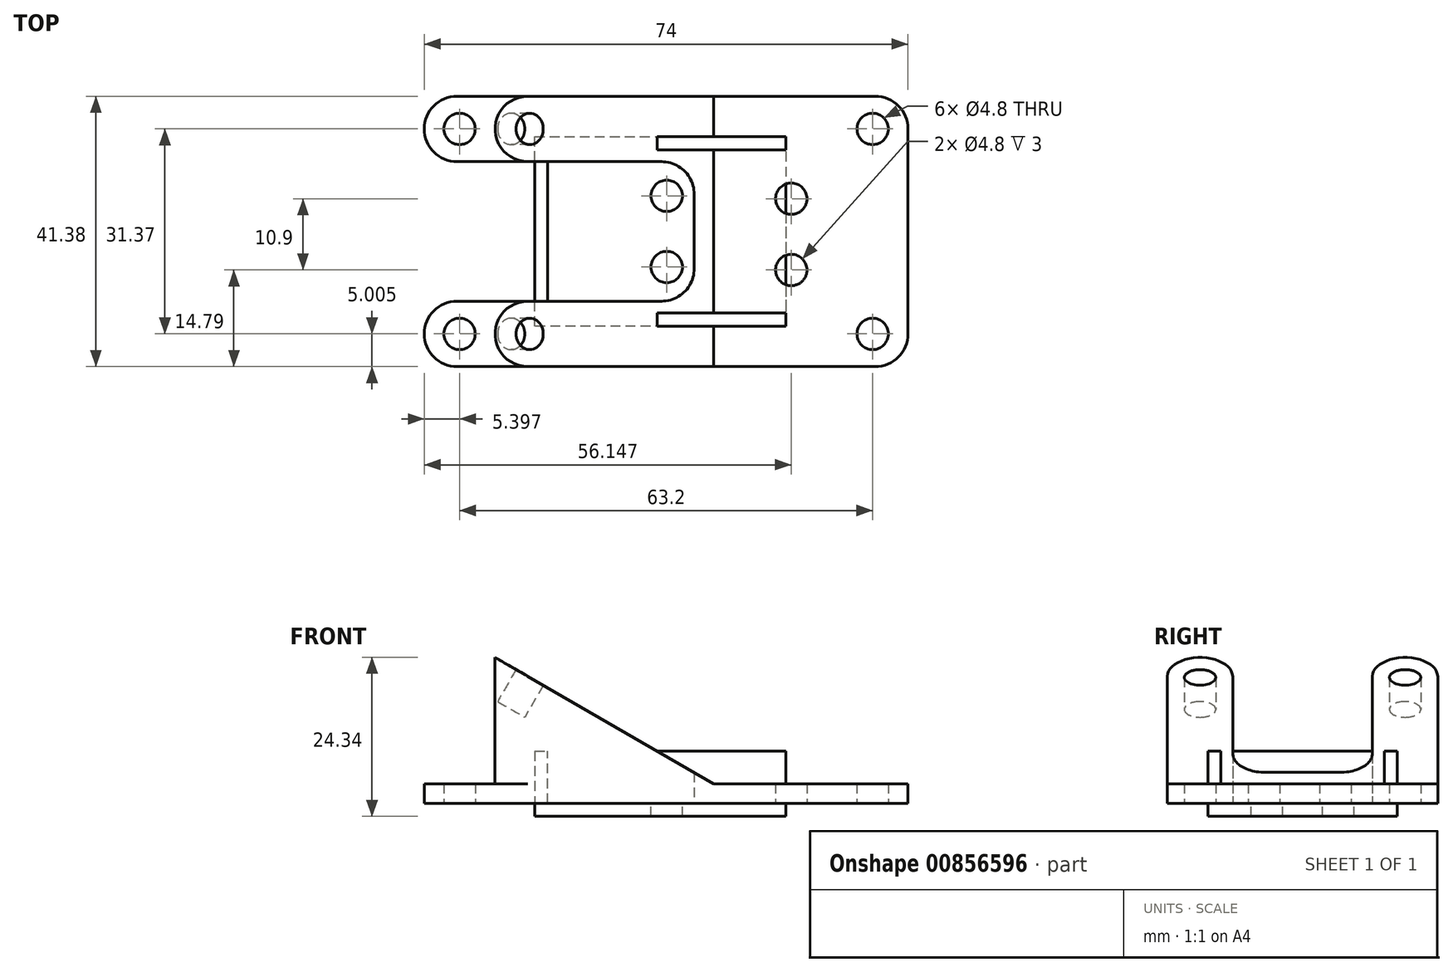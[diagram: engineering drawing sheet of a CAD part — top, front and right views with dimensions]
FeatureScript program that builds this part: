
annotation { "Feature Type Name" : "Feature", "Feature Type Description" : "" }
export const myFeature = defineFeature(function(context is Context, id is Id, definition is map)
    precondition{}
    {
        {
            var Q0;
            Q0=qCreatedBy(makeId("Top.planeOp"),FACE);
            var sketch = newSketch(context, id + "F0", { "sketchPlane" : qUnion([Q0])});
            skPoint(sketch, "E0.middle", {"position": v(0, 0) * mm});
            skCircle(sketch, "E1", {"center": v(-31.7, 15.69) * mm, "radius": 2.4 * mm});
            skLineSegment(sketch, "E2", {"start": v(-29.3, 15.69) * mm, "end": v(30.9, 15.69) * mm, "construction": true});
            skLineSegment(sketch, "E3.right", {"start": v(-37.1, 10.69) * mm, "end": v(-37.1, 20.69) * mm});
            skLineSegment(sketch, "E4", {"start": v(0, 0) * mm, "end": v(-12.47, 0) * mm, "construction": true});
            skLineSegment(sketch, "E5", {"start": v(-30.8, 9.63) * mm, "end": v(4.2, 9.63) * mm, "construction": true});
            skLineSegment(sketch, "E6", {"start": v(-37.1, 10.69) * mm, "end": v(4.2, 10.69) * mm});
            skLineSegment(sketch, "E7", {"start": v(-34.1, 15.69) * mm, "end": v(-37.1, 15.69) * mm, "construction": true});
            skCircle(sketch, "E8", {"center": v(31.5, 15.69) * mm, "radius": 2.4 * mm});
            skLineSegment(sketch, "E9.MirrorCS", {"start": v(-29.3, -15.69) * mm, "end": v(30.9, -15.69) * mm, "construction": true});
            skCircle(sketch, "E10.MirrorC", {"center": v(31.5, -15.69) * mm, "radius": 2.4 * mm});
            skLineSegment(sketch, "E11", {"start": v(33.9, 15.69) * mm, "end": v(36.9, 15.69) * mm, "construction": true});
            skLineSegment(sketch, "E12", {"start": v(-37.1, 20.69) * mm, "end": v(36.9, 20.69) * mm});
            skLineSegment(sketch, "E13.MirrorCS", {"start": v(-37.1, -10.69) * mm, "end": v(-37.1, -20.69) * mm});
            skLineSegment(sketch, "E14.MirrorCS", {"start": v(-37.1, -10.69) * mm, "end": v(4.2, -10.69) * mm});
            skLineSegment(sketch, "E15.MirrorCS", {"start": v(-37.1, -20.69) * mm, "end": v(36.9, -20.69) * mm});
            skLineSegment(sketch, "E16", {"start": v(36.9, 20.69) * mm, "end": v(36.9, -20.69) * mm});
            skLineSegment(sketch, "E17", {"start": v(4.2, 10.69) * mm, "end": v(4.2, -10.69) * mm});
            skLineSegment(sketch, "E18", {"start": v(-31.7, 18.09) * mm, "end": v(-31.7, 20.69) * mm, "construction": true});
            skLineSegment(sketch, "E19", {"start": v(-31.68, 13.29) * mm, "end": v(-31.68, 10.69) * mm, "construction": true});
            skCircle(sketch, "E20.MirrorC", {"center": v(-31.7, -15.69) * mm, "radius": 2.4 * mm});
            skLineSegment(sketch, "E21", {"start": v(4.2, 10.69) * mm, "end": v(4.2, 20.69) * mm});
            skLineSegment(sketch, "E22", {"start": v(4.2, -10.69) * mm, "end": v(4.2, -20.69) * mm});
            skLineSegment(sketch, "E23", {"start": v(-29.3, 15.69) * mm, "end": v(-26.3, 15.69) * mm});
            skLineSegment(sketch, "E24", {"start": v(-26.3, 20.69) * mm, "end": v(-26.3, 10.69) * mm});
            skLineSegment(sketch, "E25.MirrorCS", {"start": v(-26.3, -20.69) * mm, "end": v(-26.3, -10.69) * mm});
            skLineSegment(sketch, "E26", {"start": v(4.2, 15.69) * mm, "end": v(7.2, 15.69) * mm});
            skLineSegment(sketch, "E27", {"start": v(7.2, 20.69) * mm, "end": v(7.2, -20.69) * mm});
            skLineSegment(sketch, "E28", {"start": v(7.2, 15.69) * mm, "end": v(30.9, -15.69) * mm, "construction": true});
            skPoint(sketch, "E29.startSnap0", {"position": v(19.06, 0) * mm});
            skCircle(sketch, "E30", {"center": v(19.06, 5) * mm, "radius": 2.4 * mm});
            skCircle(sketch, "E31", {"center": v(19.06, -5.9) * mm, "radius": 2.4 * mm});
            skLineSegment(sketch, "E32", {"start": v(19.06, 2.6) * mm, "end": v(19.06, -3.5) * mm, "construction": true});
            skLineSegment(sketch, "E33", {"start": v(30.9, 15.69) * mm, "end": v(18.9, 15.69) * mm});
            skLineSegment(sketch, "E34.bottom", {"start": v(25.06, 10) * mm, "end": v(13.06, 10) * mm, "construction": true});
            skLineSegment(sketch, "E34.top", {"start": v(25.06, -10) * mm, "end": v(13.06, -10) * mm, "construction": true});
            skLineSegment(sketch, "E34.left", {"start": v(25.06, 10) * mm, "end": v(25.06, -10) * mm, "construction": true});
            skLineSegment(sketch, "E34.right", {"start": v(13.06, 10) * mm, "end": v(13.06, -10) * mm, "construction": true});
            skLineSegment(sketch, "E35", {"start": v(-26.3, 15.69) * mm, "end": v(-21.3, 15.69) * mm});
            skLineSegment(sketch, "E36", {"start": v(-26.3, -15.69) * mm, "end": v(-21.3, -15.69) * mm});
            skCircle(sketch, "E37", {"center": v(-21.3, 15.69) * mm, "radius": 2.4 * mm});
            skCircle(sketch, "E38", {"center": v(-21.3, -15.69) * mm, "radius": 2.4 * mm});
            skLineSegment(sketch, "E39", {"start": v(-21.3, 20.69) * mm, "end": v(-21.3, 10.69) * mm, "construction": true});
            skLineSegment(sketch, "E40", {"start": v(-21.3, -10.69) * mm, "end": v(-21.3, -20.69) * mm, "construction": true});
            skSolve(sketch);
        }
        {
            var Q0;
            {var subQ6=sQuery(id+"F0.wireOp",EDGE,"E24");var subQ9=makeQuery(id+"F0.imprint","IMPRINT",VERTEX,{"derivedFrom":subQ6});Q0=makeQuery(id+"F0.imprint","IMPRINT",FACE,{"disambiguationData":[TD([[makeQuery(id+"F0.imprint","IMPRINT",EDGE,{"disambiguationData":[TD([[subQ9,1.0]])],"derivedFrom":subQ6}),1.0]])]});}
            var Q1;
            {var subQ1=sQuery(id+"F0.wireOp",EDGE,"E17");Q1=makeQuery(id+"F0.imprint","IMPRINT",FACE,{"disambiguationData":[TD([[makeQuery(id+"F0.imprint","IMPRINT",EDGE,{"derivedFrom":subQ1}),1.0]])]});}
            var Q2;
            {var subQ5=sQuery(id+"F0.wireOp",EDGE,"E26");Q2=makeQuery(id+"F0.imprint","IMPRINT",FACE,{"disambiguationData":[TD([[makeQuery(id+"F0.imprint","IMPRINT",EDGE,{"derivedFrom":subQ5}),1.0]])]});}
            var Q3;
            {var subQ0=sQuery(id+"F0.wireOp",EDGE,"E22");Q3=makeQuery(id+"F0.imprint","IMPRINT",FACE,{"disambiguationData":[TD([[makeQuery(id+"F0.imprint","IMPRINT",EDGE,{"derivedFrom":subQ0}),-1.0]])]});}
            var Q4;
            Q4=makeQuery(id+"F0.imprint","IMPRINT",FACE,{"disambiguationData":[TD([[makeQuery(id+"F0.imprint","IMPRINT",EDGE,{"derivedFrom":sQuery(id+"F0.wireOp",EDGE,"E37")}),1.0]])]});
            var Q5;
            Q5=makeQuery(id+"F0.imprint","IMPRINT",FACE,{"disambiguationData":[TD([[makeQuery(id+"F0.imprint","IMPRINT",EDGE,{"derivedFrom":sQuery(id+"F0.wireOp",EDGE,"E38")}),1.0]])]});
            extrude(context, id + "F1", {"entities" : qUnion([Q0, Q1, Q2, Q3, Q4, Q5]), "depth" : 25 * mm, "offsetDistance" : 25 * mm});
        }
        {
            var Q0;
            Q0=makeQuery(id+"F0.imprint","IMPRINT",FACE,{"disambiguationData":[TD([[makeQuery(id+"F0.imprint","IMPRINT",EDGE,{"derivedFrom":sQuery(id+"F0.wireOp",EDGE,"E1")}),-1.0]])]});
            var Q1;
            {var subQ1=sQuery(id+"F0.wireOp",EDGE,"E13.MirrorCS");Q1=makeQuery(id+"F0.imprint","IMPRINT",FACE,{"disambiguationData":[TD([[makeQuery(id+"F0.imprint","IMPRINT",EDGE,{"derivedFrom":subQ1}),1.0]])]});}
            var Q2;
            Q2=makeQuery(id+"F0.imprint","IMPRINT",FACE,{"disambiguationData":[TD([[makeQuery(id+"F0.imprint","IMPRINT",EDGE,{"derivedFrom":sQuery(id+"F0.wireOp",EDGE,"E8")}),-1.0]])]});
            extrude(context, id + "F2", {"entities" : qUnion([Q0, Q1, Q2]), "operationType" : NewBodyOperationType.ADD, "depth" : 3 * mm, "offsetDistance" : 25 * mm});
        }
        {
            var Q0;
            Q0=makeQuery(id+"F1.opExtrude","CAP_EDGE",EDGE,{"disambiguationData":[OSD([sQuery(id+"F0.wireOp",EDGE,"E27")])],"isStart":false});
            chamfer(context, id + "F3", {"entities" : qUnion([Q0]), "chamferType" : ChamferType.OFFSET_ANGLE, "width" : 22 * mm, "oppositeDirection" : false, "angle" : 60 * degree, "tangentPropagation" : true});
        }
        {
            var Q0;
            Q0=makeQuery(id+"F2.opExtrude","SWEPT_EDGE",EDGE,{"disambiguationData":[OSD([sQuery(id+"F0.wireOp",EDGE,"E3.right"),sQuery(id+"F0.wireOp",EDGE,"E12")])]});
            var Q1;
            Q1=makeQuery(id+"F2.opExtrude","SWEPT_EDGE",EDGE,{"disambiguationData":[OSD([sQuery(id+"F0.wireOp",EDGE,"E3.right"),sQuery(id+"F0.wireOp",EDGE,"E6")])]});
            var Q2;
            Q2=makeQuery(id+"F2.opExtrude","SWEPT_EDGE",EDGE,{"disambiguationData":[OSD([sQuery(id+"F0.wireOp",EDGE,"E13.MirrorCS"),sQuery(id+"F0.wireOp",EDGE,"E14.MirrorCS")])]});
            var Q3;
            Q3=makeQuery(id+"F2.opExtrude","SWEPT_EDGE",EDGE,{"disambiguationData":[OSD([sQuery(id+"F0.wireOp",EDGE,"E13.MirrorCS"),sQuery(id+"F0.wireOp",EDGE,"E15.MirrorCS")])]});
            var Q4;
            Q4=makeQuery(id+"F2.opExtrude","SWEPT_EDGE",EDGE,{"disambiguationData":[OSD([sQuery(id+"F0.wireOp",EDGE,"E15.MirrorCS"),sQuery(id+"F0.wireOp",EDGE,"E16")])]});
            var Q5;
            Q5=makeQuery(id+"F2.opExtrude","SWEPT_EDGE",EDGE,{"disambiguationData":[OSD([sQuery(id+"F0.wireOp",EDGE,"E12"),sQuery(id+"F0.wireOp",EDGE,"E16")])]});
            fillet(context, id + "F4", {"entities" : qUnion([Q0, Q1, Q2, Q3, Q4, Q5]), "radius" : 5 * mm, "tangentPropagation" : true, "allowEdgeOverflow" : false});
        }
        {
            var Q0;
            Q0=makeQuery(id+"F1.opExtrude","SWEPT_EDGE",EDGE,{"disambiguationData":[OSD([sQuery(id+"F0.wireOp",EDGE,"E12"),sQuery(id+"F0.wireOp",EDGE,"E24")])]});
            var Q1;
            Q1=makeQuery(id+"F1.opExtrude","SWEPT_EDGE",EDGE,{"disambiguationData":[OSD([sQuery(id+"F0.wireOp",EDGE,"E6"),sQuery(id+"F0.wireOp",EDGE,"E24")])]});
            var Q2;
            Q2=makeQuery(id+"F1.opExtrude","SWEPT_EDGE",EDGE,{"disambiguationData":[OSD([sQuery(id+"F0.wireOp",EDGE,"E14.MirrorCS"),sQuery(id+"F0.wireOp",EDGE,"E25.MirrorCS")])]});
            var Q3;
            Q3=makeQuery(id+"F1.opExtrude","SWEPT_EDGE",EDGE,{"disambiguationData":[OSD([sQuery(id+"F0.wireOp",EDGE,"E15.MirrorCS"),sQuery(id+"F0.wireOp",EDGE,"E25.MirrorCS")])]});
            fillet(context, id + "F5", {"entities" : qUnion([Q0, Q1, Q2, Q3]), "radius" : 5 * mm, "tangentPropagation" : true, "allowEdgeOverflow" : false});
        }
        {
            var Q0;
            Q0=makeQuery(id+"F1.opExtrude","SWEPT_EDGE",EDGE,{"disambiguationData":[OSD([sQuery(id+"F0.wireOp",EDGE,"E6"),sQuery(id+"F0.wireOp",EDGE,"E17"),sQuery(id+"F0.wireOp",EDGE,"E21")])]});
            var Q1;
            Q1=makeQuery(id+"F1.opExtrude","SWEPT_EDGE",EDGE,{"disambiguationData":[OSD([sQuery(id+"F0.wireOp",EDGE,"E14.MirrorCS"),sQuery(id+"F0.wireOp",EDGE,"E17"),sQuery(id+"F0.wireOp",EDGE,"E22")])]});
            fillet(context, id + "F6", {"entities" : qUnion([Q0, Q1]), "radius" : 5 * mm, "tangentPropagation" : true, "allowEdgeOverflow" : false});
        }
        {
            var Q0;
            Q0=qCreatedBy(makeId("Top.planeOp"),FACE);
            var sketch = newSketch(context, id + "F7", { "sketchPlane" : qUnion([Q0])});
            skLineSegment(sketch, "E41", {"start": v(0, 5.45) * mm, "end": v(0, -5.45) * mm, "construction": true});
            skCircle(sketch, "E42", {"center": v(0, 5.45) * mm, "radius": 2.4 * mm});
            skCircle(sketch, "E43", {"center": v(0, -5.45) * mm, "radius": 2.4 * mm});
            skPoint(sketch, "E44.middle", {"position": v(0, 0) * mm});
            skLineSegment(sketch, "E45", {"start": v(0, 0) * mm, "end": v(-29.75, 0) * mm, "construction": true});
            skLineSegment(sketch, "E46.bottom", {"start": v(18.2, -12.5) * mm, "end": v(-18.2, -12.5) * mm});
            skLineSegment(sketch, "E46.top", {"start": v(18.2, 12.5) * mm, "end": v(-18.2, 12.5) * mm});
            skLineSegment(sketch, "E46.left", {"start": v(18.2, -12.5) * mm, "end": v(18.2, 12.5) * mm});
            skLineSegment(sketch, "E46.right", {"start": v(-18.2, -12.5) * mm, "end": v(-18.2, 12.5) * mm});
            skLineSegment(sketch, "E47.3", {"start": v(-20.2, -14.5) * mm, "end": v(-20.2, 14.5) * mm});
            skLineSegment(sketch, "E48", {"start": v(-20.2, 14.5) * mm, "end": v(-18.2, 12.5) * mm, "construction": true});
            skLineSegment(sketch, "E49", {"start": v(-18.2, -12.5) * mm, "end": v(-20.2, -14.5) * mm, "construction": true});
            skLineSegment(sketch, "E50", {"start": v(18.2, 12.5) * mm, "end": v(18.2, 14.5) * mm});
            skLineSegment(sketch, "E51", {"start": v(18.2, -12.5) * mm, "end": v(18.2, -14.5) * mm});
            skLineSegment(sketch, "E52", {"start": v(-20.2, 14.5) * mm, "end": v(18.2, 14.5) * mm});
            skLineSegment(sketch, "E53", {"start": v(18.2, -14.5) * mm, "end": v(-20.2, -14.5) * mm});
            skCircle(sketch, "E54.0", {"center": v(0, 5.45) * mm, "radius": 4.4 * mm});
            skCircle(sketch, "E55.0", {"center": v(0, -5.45) * mm, "radius": 4.4 * mm});
            skSolve(sketch);
        }
        {
            var Q0;
            Q0=makeQuery(id+"F0.imprint","IMPRINT",FACE,{"disambiguationData":[TD([[makeQuery(id+"F0.imprint","IMPRINT",EDGE,{"derivedFrom":sQuery(id+"F0.wireOp",EDGE,"E37")}),1.0]])]});
            var Q1;
            Q1=makeQuery(id+"F0.imprint","IMPRINT",FACE,{"disambiguationData":[TD([[makeQuery(id+"F0.imprint","IMPRINT",EDGE,{"derivedFrom":sQuery(id+"F0.wireOp",EDGE,"E38")}),1.0]])]});
            extrude(context, id + "F8", {"entities" : qUnion([Q0, Q1]), "endBound" : BoundingType.SYMMETRIC, "depth" : 10 * mm, "offsetDistance" : 25 * mm});
        }
        {
            var Q0;
            Q0=makeQuery(id+"F8.opExtrude","SWEPT_BODY",BODY,{"disambiguationData":[OSD([sQuery(id+"F0.wireOp",EDGE,"E38")])]});
            var Q1;
            Q1=sQuery(id+"F0.wireOp",EDGE,"E40");
            transform(context, id + "F9", {"entities" : qUnion([Q0]), "transformType" : TransformType.ROTATION, "transformAxis" : qUnion([Q1]), "angle" : 30 * degree, "oppositeDirection" : true, "makeCopy" : false});
        }
        {
            var Q0;
            Q0=makeQuery(id+"F8.opExtrude","SWEPT_BODY",BODY,{"disambiguationData":[OSD([sQuery(id+"F0.wireOp",EDGE,"E37")])]});
            var Q1;
            Q1=sQuery(id+"F0.wireOp",EDGE,"E39");
            transform(context, id + "F10", {"entities" : qUnion([Q0]), "transformType" : TransformType.ROTATION, "transformAxis" : qUnion([Q1]), "angle" : 30 * degree, "oppositeDirection" : true, "makeCopy" : false});
        }
        {
            var Q0;
            Q0=makeQuery(id+"F8.opExtrude","SWEPT_BODY",BODY,{"disambiguationData":[OSD([sQuery(id+"F0.wireOp",EDGE,"E38")])]});
            var Q1;
            Q1=makeQuery(id+"F8.opExtrude","SWEPT_BODY",BODY,{"disambiguationData":[OSD([sQuery(id+"F0.wireOp",EDGE,"E37")])]});
            var Q2;
            {var subQ0=sQuery(id+"F0.wireOp",EDGE,"E15.MirrorCS");var subQ1=sQuery(id+"F0.wireOp",EDGE,"E25.MirrorCS");Q2=makeQuery(id+"F5.opFillet","BLEND_EDGE",EDGE,{"blendedFrom":[makeQuery(id+"F1.opExtrude","SWEPT_EDGE",EDGE,{"disambiguationData":[OSD([subQ0,subQ1])]}),makeQuery(id+"F2.boolean.opBoolean","MERGE",FACE,{"derivedFrom":[makeQuery(id+"F1.opExtrude","SWEPT_FACE",FACE,{"disambiguationData":[OSD([subQ0])]}),makeQuery(id+"F2.opExtrude","SWEPT_FACE",FACE,{"disambiguationData":[OSD([subQ0]),TDD([makeQuery(id+"F0.imprint","IMPRINT",EDGE,{"disambiguationData":[TD([[makeQuery(id+"F0.imprint","INTERSECT",VERTEX,{"derivedFrom":[sQuery(id+"F0.wireOp",EDGE,"E13.MirrorCS"),subQ0]}),-1.0]])],"derivedFrom":subQ0})])]}),makeQuery(id+"F2.opExtrude","SWEPT_FACE",FACE,{"disambiguationData":[OSD([subQ0]),TDD([makeQuery(id+"F0.imprint","IMPRINT",EDGE,{"disambiguationData":[TD([[makeQuery(id+"F0.imprint","INTERSECT",VERTEX,{"derivedFrom":[subQ0,sQuery(id+"F0.wireOp",EDGE,"E16")]}),1.0]])],"derivedFrom":subQ0})])]})]})],"blendedInto":[makeQuery(id+"F2.boolean.opBoolean","MERGE",FACE,{"derivedFrom":[makeQuery(id+"F1.opExtrude","SWEPT_FACE",FACE,{"disambiguationData":[OSD([subQ0])]}),makeQuery(id+"F2.opExtrude","SWEPT_FACE",FACE,{"disambiguationData":[OSD([subQ0]),TDD([makeQuery(id+"F0.imprint","IMPRINT",EDGE,{"disambiguationData":[TD([[makeQuery(id+"F0.imprint","INTERSECT",VERTEX,{"derivedFrom":[sQuery(id+"F0.wireOp",EDGE,"E13.MirrorCS"),subQ0]}),-1.0]])],"derivedFrom":subQ0})])]}),makeQuery(id+"F2.opExtrude","SWEPT_FACE",FACE,{"disambiguationData":[OSD([subQ0]),TDD([makeQuery(id+"F0.imprint","IMPRINT",EDGE,{"disambiguationData":[TD([[makeQuery(id+"F0.imprint","INTERSECT",VERTEX,{"derivedFrom":[subQ0,sQuery(id+"F0.wireOp",EDGE,"E16")]}),1.0]])],"derivedFrom":subQ0})])]})]})]});}
            transform(context, id + "F11", {"entities" : qUnion([Q0, Q1]), "transformType" : TransformType.TRANSLATION_DISTANCE, "transformDirection" : qUnion([Q2]), "distance" : 18.7 * mm, "oppositeDirection" : true, "makeCopy" : false});
        }
        {
            var Q0;
            Q0=makeQuery(id+"F8.opExtrude","SWEPT_BODY",BODY,{"disambiguationData":[OSD([sQuery(id+"F0.wireOp",EDGE,"E37")])]});
            var Q1;
            Q1=makeQuery(id+"F8.opExtrude","SWEPT_BODY",BODY,{"disambiguationData":[OSD([sQuery(id+"F0.wireOp",EDGE,"E38")])]});
            var Q2;
            Q2=makeQuery(id+"F1.opExtrude","SWEPT_BODY",BODY,{"disambiguationData":[OSD([sQuery(id+"F0.wireOp",EDGE,"E6"),sQuery(id+"F0.wireOp",EDGE,"E12"),sQuery(id+"F0.wireOp",EDGE,"E14.MirrorCS"),sQuery(id+"F0.wireOp",EDGE,"E15.MirrorCS"),sQuery(id+"F0.wireOp",EDGE,"E17"),sQuery(id+"F0.wireOp",EDGE,"E24"),sQuery(id+"F0.wireOp",EDGE,"E25.MirrorCS"),sQuery(id+"F0.wireOp",EDGE,"E27")])]});
            booleanBodies(context, id + "F12", {"operationType" : BooleanOperationType.SUBTRACTION, "tools" : qUnion([Q0, Q1]), "targets" : qUnion([Q2])});
        }
        {
            var Q0;
            Q0=makeQuery(id+"F7.imprint","IMPRINT",FACE,{"disambiguationData":[TD([[makeQuery(id+"F7.imprint","IMPRINT",EDGE,{"derivedFrom":sQuery(id+"F7.wireOp",EDGE,"E46.bottom")}),1.0]])]});
            var Q1;
            Q1=makeQuery(id+"F7.imprint","IMPRINT",FACE,{"disambiguationData":[TD([[makeQuery(id+"F7.imprint","IMPRINT",EDGE,{"derivedFrom":sQuery(id+"F7.wireOp",EDGE,"E46.bottom")}),-1.0]])]});
            var Q2;
            Q2=makeQuery(id+"F7.imprint","IMPRINT",FACE,{"disambiguationData":[TD([[makeQuery(id+"F7.imprint","IMPRINT",EDGE,{"derivedFrom":sQuery(id+"F7.wireOp",EDGE,"E42")}),-1.0]])]});
            var Q3;
            Q3=makeQuery(id+"F7.imprint","IMPRINT",FACE,{"disambiguationData":[TD([[makeQuery(id+"F7.imprint","IMPRINT",EDGE,{"derivedFrom":sQuery(id+"F7.wireOp",EDGE,"E43")}),-1.0]])]});
            extrude(context, id + "F13", {"entities" : qUnion([Q0, Q1, Q2, Q3]), "oppositeDirection" : true, "depth" : 2 * mm, "offsetDistance" : 25 * mm});
        }
        {
            var Q0;
            Q0=makeQuery(id+"F7.imprint","IMPRINT",FACE,{"disambiguationData":[TD([[makeQuery(id+"F7.imprint","IMPRINT",EDGE,{"derivedFrom":sQuery(id+"F7.wireOp",EDGE,"E46.bottom")}),1.0]])]});
            extrude(context, id + "F14", {"entities" : qUnion([Q0]), "operationType" : NewBodyOperationType.ADD, "depth" : 8 * mm, "offsetDistance" : 25 * mm});
        }
    });
